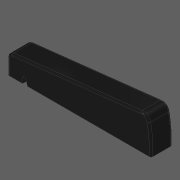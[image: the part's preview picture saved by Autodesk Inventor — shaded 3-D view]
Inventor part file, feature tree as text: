
AUTODESK INVENTOR PART (.ipt)
format: ipt  version: 2020 (Build 240168000, 168)  size: 258,048 bytes
history: native  units: in
note: dims shown in document units (in); Inventor stores cm internally (conversion verified against a paired STEP export)
features: other x3, extrude x3, fillet x2
ambient origin geometry x8: Origin, YZ Plane, XZ Plane, XY Plane, X Axis, Y Axis, Z Axis, Center Point
bodies: Solid1 (feature_tree)
feature tree (8):
  other  "Slot Start Plane"
  other  "Key Profile"
  extrude  "Key"  Depth=0.063in
  extrude  "Protrusion Cutout"  TaperAngle=0.0deg  [1 undecoded]
  fillet  "Front Fillet"  [1 undecoded]
  extrude  "Slot"  Depth=0.1181in
  fillet  "Edge Softening"  Radius=0.1374in
  other  "Slot Sketch"
note: 2 required parameter values undecoded (feature->parameter linkage not recoverable at this tier; creation-order binding heuristic only, values carry confidence <= 0.55)
